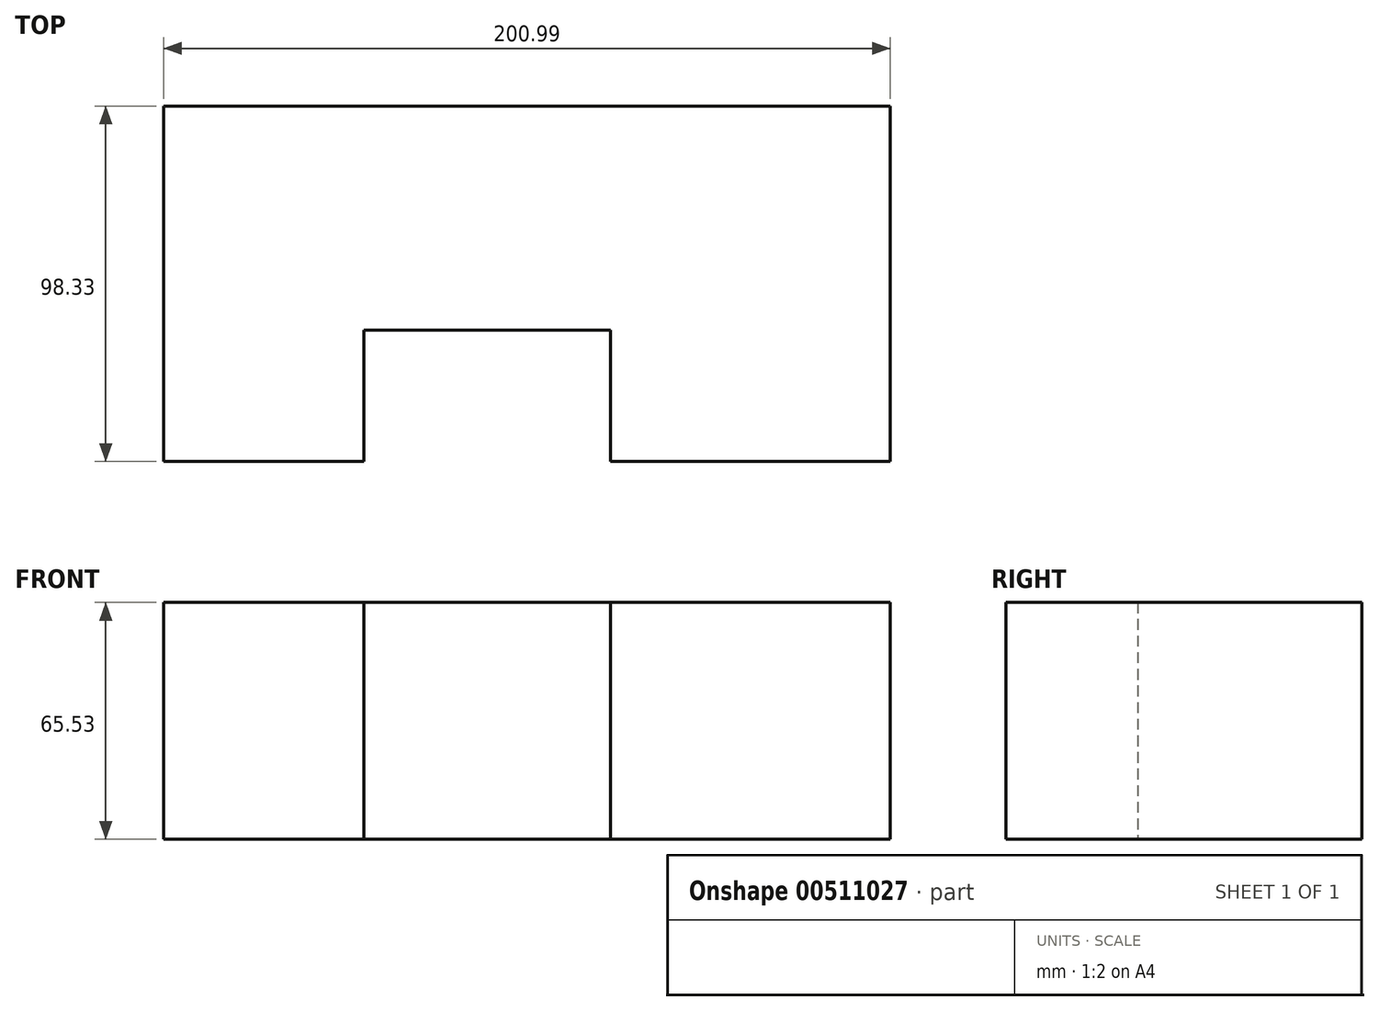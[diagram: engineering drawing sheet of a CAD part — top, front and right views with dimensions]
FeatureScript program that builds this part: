
annotation { "Feature Type Name" : "Feature", "Feature Type Description" : "" }
export const myFeature = defineFeature(function(context is Context, id is Id, definition is map)
    precondition{}
    {
        {
            var Q0;
            Q0=qCreatedBy(makeId("Top.planeOp"),FACE);
            var sketch = newSketch(context, id + "F0", { "sketchPlane" : qUnion([Q0])});
            skLineSegment(sketch, "E0.bottom", {"start": v(-93.5, 61.94) * mm, "end": v(107.48, 61.94) * mm});
            skLineSegment(sketch, "E0.top", {"start": v(-93.5, -36.4) * mm, "end": v(107.48, -36.4) * mm});
            skLineSegment(sketch, "E0.left", {"start": v(-93.5, 61.94) * mm, "end": v(-93.5, -36.4) * mm});
            skLineSegment(sketch, "E0.right", {"start": v(107.48, 61.94) * mm, "end": v(107.48, -36.4) * mm});
            skLineSegment(sketch, "E1", {"start": v(-38.08, -36.4) * mm, "end": v(-38.08, 0) * mm});
            skLineSegment(sketch, "E2", {"start": v(-38.08, 0) * mm, "end": v(30.12, 0) * mm});
            skLineSegment(sketch, "E3", {"start": v(30.12, 0) * mm, "end": v(30.12, -36.4) * mm});
            skLineSegment(sketch, "E4", {"start": v(30.12, -36.4) * mm, "end": v(30.12, -38.56) * mm});
            skSolve(sketch);
        }
        {
            var Q0;
            Q0=makeQuery(id+"F0.imprint","IMPRINT",FACE,{"disambiguationData":[TD([[makeQuery(id+"F0.imprint","IMPRINT",EDGE,{"derivedFrom":sQuery(id+"F0.wireOp",EDGE,"E0.bottom")}),-1.0]])]});
            extrude(context, id + "F1", {"entities" : qUnion([Q0]), "depth" : 65.53 * mm});
        }
    });
